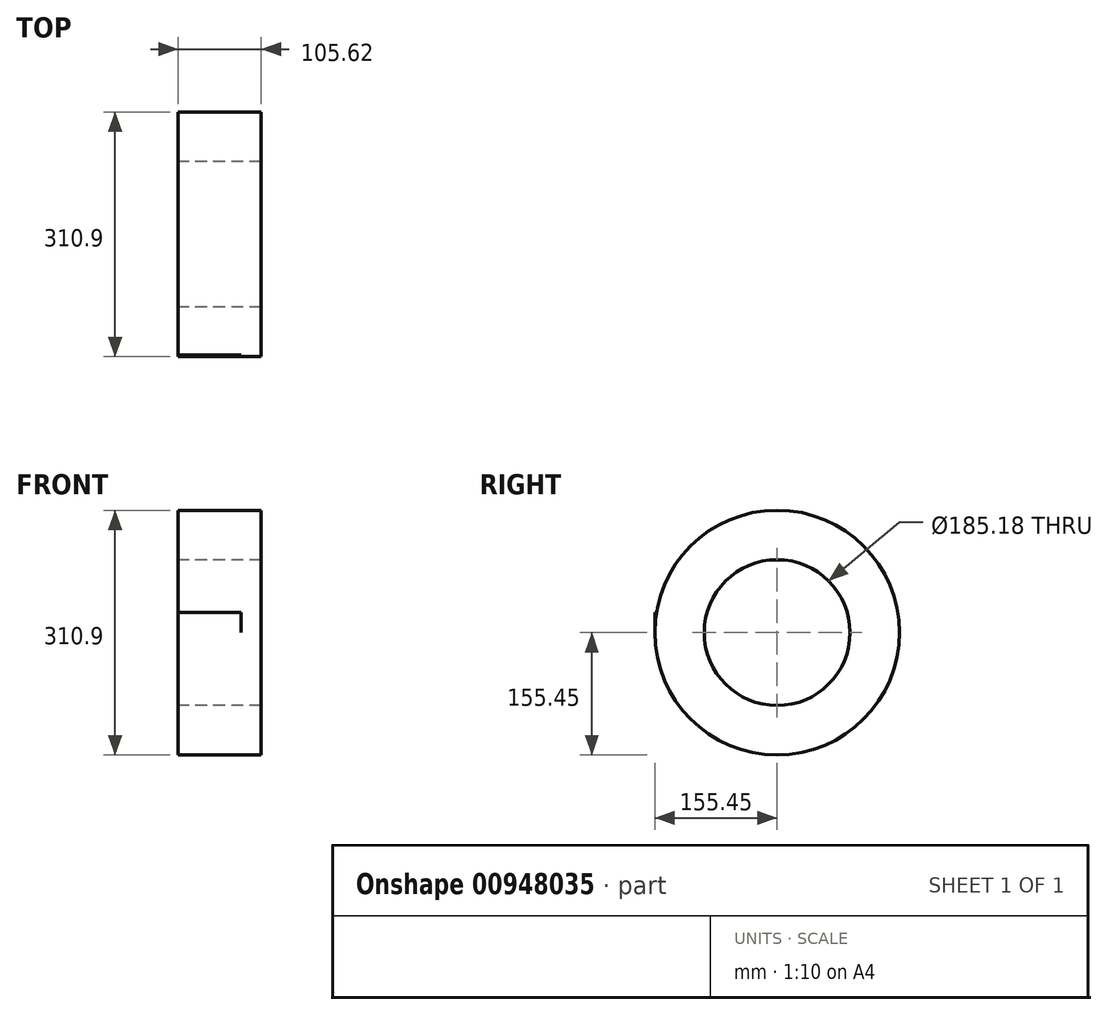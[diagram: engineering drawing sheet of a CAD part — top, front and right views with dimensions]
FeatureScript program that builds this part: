
annotation { "Feature Type Name" : "Feature", "Feature Type Description" : "" }
export const myFeature = defineFeature(function(context is Context, id is Id, definition is map)
    precondition{}
    {
        {
            var Q0;
            Q0=qCreatedBy(makeId("Top.planeOp"),FACE);
            var sketch = newSketch(context, id + "F0", { "sketchPlane" : qUnion([Q0])});
            skLineSegment(sketch, "E0.bottom", {"start": v(0, 0) * mm, "end": v(105.62, 0) * mm});
            skLineSegment(sketch, "E0.top", {"start": v(0, -62.86) * mm, "end": v(105.62, -62.86) * mm});
            skLineSegment(sketch, "E0.left", {"start": v(0, 0) * mm, "end": v(0, -62.86) * mm});
            skLineSegment(sketch, "E0.right", {"start": v(105.62, 0) * mm, "end": v(105.62, -62.86) * mm});
            skSolve(sketch);
        }
        {
            var Q0;
            Q0=makeQuery(id+"F0.imprint","IMPRINT",FACE,{"disambiguationData":[TD([[makeQuery(id+"F0.imprint","IMPRINT",EDGE,{"derivedFrom":sQuery(id+"F0.wireOp",EDGE,"E0.bottom")}),-1.0]])]});
            extrude(context, id + "F1", {"entities" : qUnion([Q0]), "depth" : 25.4 * mm, "offsetDistance" : 25.4 * mm});
        }
        {
            var Q0;
            Q0=qCreatedBy(makeId("Right.planeOp"),FACE);
            var sketch = newSketch(context, id + "F2", { "sketchPlane" : qUnion([Q0])});
            skCircle(sketch, "E1", {"center": v(92.59, 0) * mm, "radius": 10.82 * mm});
            skSolve(sketch);
        }
        {
            var Q0;
            Q0=makeQuery(id+"F1.opExtrude","CAP_FACE",FACE,{"disambiguationData":[OSD([sQuery(id+"F0.wireOp",EDGE,"E0.bottom"),sQuery(id+"F0.wireOp",EDGE,"E0.top"),sQuery(id+"F0.wireOp",EDGE,"E0.left"),sQuery(id+"F0.wireOp",EDGE,"E0.right")])],"isStart":true});
            var Q1;
            Q1=sQuery(id+"F2.wireOp",EDGE,"E1");
            revolve(context, id + "F3", {"operationType" : NewBodyOperationType.ADD, "surfaceOperationType" : NewSurfaceOperationType.NEW, "entities" : qUnion([Q0]), "axis" : qUnion([Q1]), "revolveType" : RevolveType.FULL});
        }
        {
            var Q0;
            {var subQ0=sQuery(id+"F0.wireOp",EDGE,"E0.right");Q0=makeQuery(id+"F3.boolean.opBoolean","MERGE",FACE,{"derivedFrom":[makeQuery(id+"F1.opExtrude","SWEPT_FACE",FACE,{"disambiguationData":[OSD([subQ0])]}),makeQuery(id+"F3.opRevolve","SWEPT_FACE",FACE,{"disambiguationData":[OSD([subQ0])]})]});}
            var sketch = newSketch(context, id + "F4", { "sketchPlane" : qUnion([Q0])});
            skArc(sketch, "E2", {"start": v(-60.77, 25.4) * mm, "mid": v(-62.34, 12.74) * mm, "end": v(-62.86, 0) * mm});
            skSolve(sketch);
        }
        {
            var Q0;
            Q0=makeQuery(id+"F4.imprint","IMPRINT",FACE,{"disambiguationData":[TD([[makeQuery(id+"F4.imprint","IMPRINT",EDGE,{"derivedFrom":sQuery(id+"F4.wireOp",EDGE,"E2")}),-1.0]])]});
            extrude(context, id + "F5", {"entities" : qUnion([Q0]), "operationType" : NewBodyOperationType.REMOVE, "oppositeDirection" : true, "depth" : 25.4 * mm, "offsetDistance" : 25.4 * mm});
        }
    });
